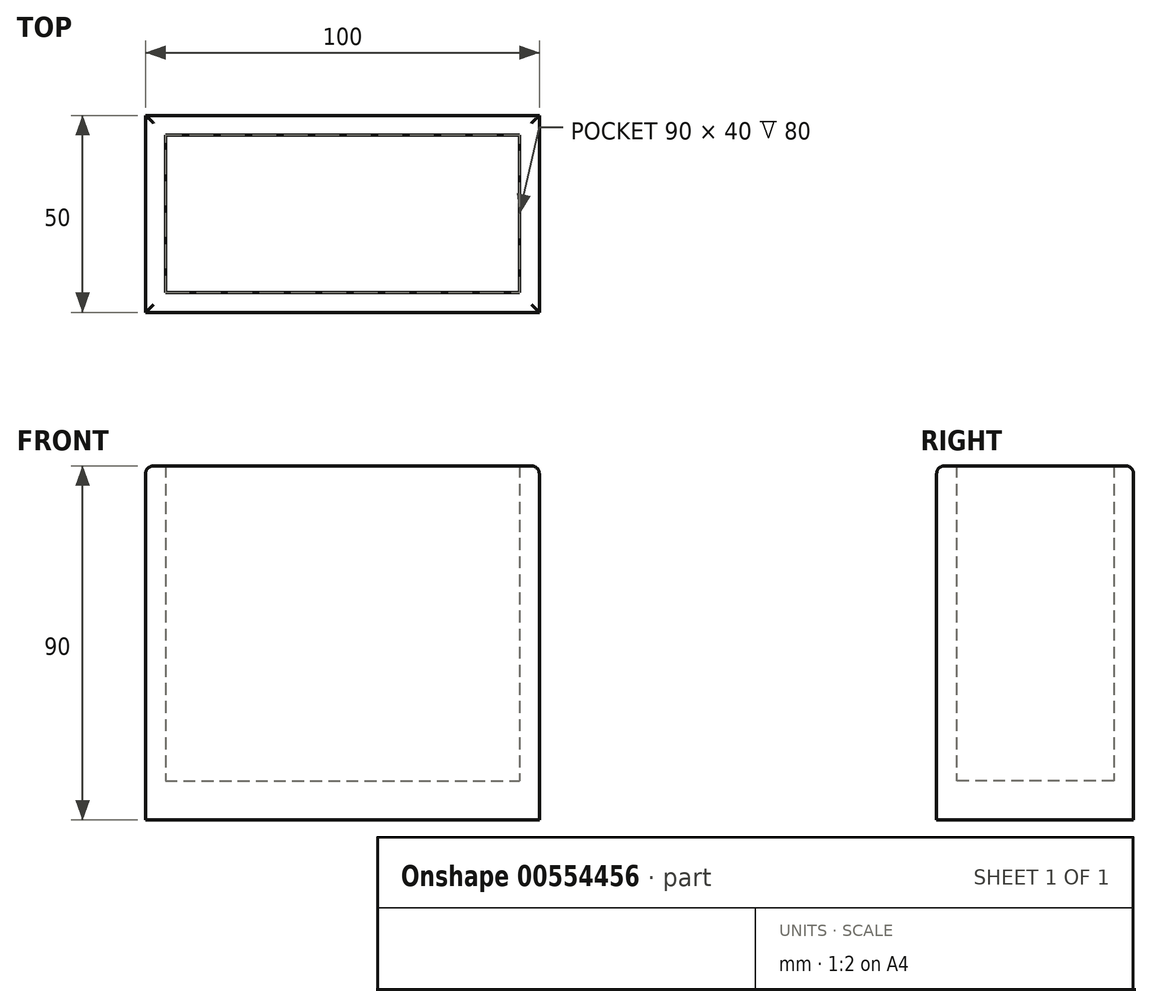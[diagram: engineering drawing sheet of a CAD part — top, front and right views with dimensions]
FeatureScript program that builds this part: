
annotation { "Feature Type Name" : "Feature", "Feature Type Description" : "" }
export const myFeature = defineFeature(function(context is Context, id is Id, definition is map)
    precondition{}
    {
        {
            var Q0;
            Q0=qCreatedBy(makeId("Top.planeOp"),FACE);
            var sketch = newSketch(context, id + "F0", { "sketchPlane" : qUnion([Q0])});
            skLineSegment(sketch, "E0.bottom", {"start": v(50, -25) * mm, "end": v(-50, -25) * mm});
            skLineSegment(sketch, "E0.top", {"start": v(50, 25) * mm, "end": v(-50, 25) * mm});
            skLineSegment(sketch, "E0.left", {"start": v(50, -25) * mm, "end": v(50, 25) * mm});
            skLineSegment(sketch, "E0.right", {"start": v(-50, -25) * mm, "end": v(-50, 25) * mm});
            skPoint(sketch, "E0.middle", {"position": v(0, 0) * mm});
            skSolve(sketch);
        }
        {
            var Q0;
            Q0 = qSketchRegion(id + "F0", true);
            extrude(context, id + "F1", {"entities" : qUnion([Q0]), "depth" : 10 * mm, "offsetDistance" : 25 * mm});
        }
        {
            var Q0;
            Q0=makeQuery(id+"F1.opExtrude","CAP_FACE",FACE,{"disambiguationData":[OSD([sQuery(id+"F0.wireOp",EDGE,"E0.bottom"),sQuery(id+"F0.wireOp",EDGE,"E0.top"),sQuery(id+"F0.wireOp",EDGE,"E0.left"),sQuery(id+"F0.wireOp",EDGE,"E0.right")])],"isStart":false});
            var sketch = newSketch(context, id + "F2", { "sketchPlane" : qUnion([Q0])});
            skLineSegment(sketch, "E1.bottom", {"start": v(-45, 20) * mm, "end": v(45, 20) * mm});
            skLineSegment(sketch, "E1.top", {"start": v(-45, -20) * mm, "end": v(45, -20) * mm});
            skLineSegment(sketch, "E1.left", {"start": v(-45, 20) * mm, "end": v(-45, -20) * mm});
            skLineSegment(sketch, "E1.right", {"start": v(45, 20) * mm, "end": v(45, -20) * mm});
            skLineSegment(sketch, "E2", {"start": v(-50, -25) * mm, "end": v(-50, 25) * mm});
            skLineSegment(sketch, "E3", {"start": v(-50, 25) * mm, "end": v(50, 25) * mm});
            skLineSegment(sketch, "E4", {"start": v(50, 25) * mm, "end": v(50, -25) * mm});
            skLineSegment(sketch, "E5", {"start": v(50, -25) * mm, "end": v(-50, -25) * mm});
            skSolve(sketch);
        }
        {
            var Q0;
            Q0=makeQuery(id+"F2.imprint","IMPRINT",FACE,{"disambiguationData":[TD([[makeQuery(id+"F2.imprint","IMPRINT",EDGE,{"derivedFrom":sQuery(id+"F2.wireOp",EDGE,"E1.bottom")}),1.0]])]});
            extrude(context, id + "F3", {"entities" : qUnion([Q0]), "operationType" : NewBodyOperationType.ADD, "depth" : 80 * mm, "offsetDistance" : 25 * mm});
        }
        {
            var Q0;
            Q0=makeQuery(id+"F3.opExtrude","CAP_EDGE",EDGE,{"disambiguationData":[OSD([sQuery(id+"F2.wireOp",EDGE,"E3")])],"isStart":false});
            var Q1;
            Q1=makeQuery(id+"F3.opExtrude","CAP_EDGE",EDGE,{"disambiguationData":[OSD([sQuery(id+"F2.wireOp",EDGE,"E5")])],"isStart":false});
            var Q2;
            Q2=makeQuery(id+"F3.opExtrude","CAP_EDGE",EDGE,{"disambiguationData":[OSD([sQuery(id+"F2.wireOp",EDGE,"E2")])],"isStart":false});
            var Q3;
            Q3=makeQuery(id+"F3.opExtrude","CAP_EDGE",EDGE,{"disambiguationData":[OSD([sQuery(id+"F2.wireOp",EDGE,"E4")])],"isStart":false});
            fillet(context, id + "F4", {"entities" : qUnion([Q0, Q1, Q2, Q3]), "radius" : 2 * mm, "tangentPropagation" : true, "allowEdgeOverflow" : false});
        }
    });
